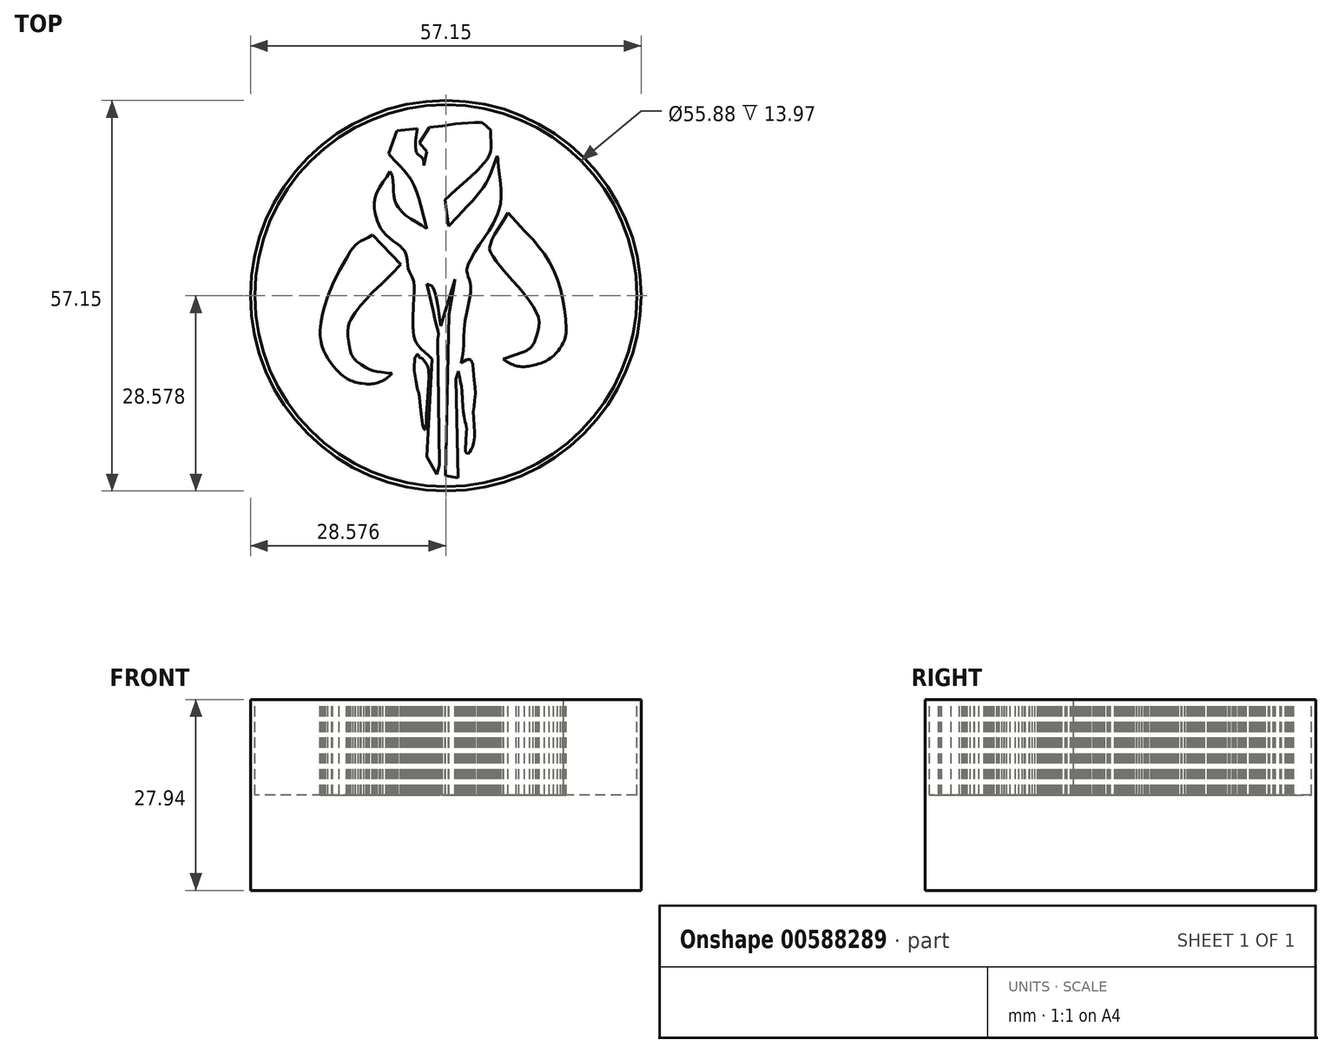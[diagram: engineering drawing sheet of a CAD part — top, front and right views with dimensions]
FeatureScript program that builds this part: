
annotation { "Feature Type Name" : "Feature", "Feature Type Description" : "" }
export const myFeature = defineFeature(function(context is Context, id is Id, definition is map)
    precondition{}
    {
        {
            var Q0;
            Q0=qCreatedBy(makeId("Top.planeOp"),FACE);
            var sketch = newSketch(context, id + "F0", { "sketchPlane" : qUnion([Q0])});
            skLineSegment(sketch, "E0", {"start": v(-3.17, -5.44) * mm, "end": v(-3.05, -5.48) * mm});
            skLineSegment(sketch, "E1", {"start": v(-3.05, -5.48) * mm, "end": v(-3, -5.51) * mm});
            skLineSegment(sketch, "E2", {"start": v(-3, -5.51) * mm, "end": v(-2.97, -5.54) * mm});
            skLineSegment(sketch, "E3", {"start": v(-2.97, -5.54) * mm, "end": v(-2.94, -5.6) * mm});
            skLineSegment(sketch, "E4", {"start": v(-2.94, -5.6) * mm, "end": v(-2.93, -5.66) * mm});
            skLineSegment(sketch, "E5", {"start": v(-2.93, -5.66) * mm, "end": v(-2.91, -5.76) * mm});
            skLineSegment(sketch, "E6", {"start": v(-2.91, -5.76) * mm, "end": v(-2.89, -5.81) * mm});
            skLineSegment(sketch, "E7", {"start": v(-2.89, -5.81) * mm, "end": v(-2.85, -5.86) * mm});
            skLineSegment(sketch, "E8", {"start": v(-2.85, -5.86) * mm, "end": v(-2.75, -5.91) * mm});
            skLineSegment(sketch, "E9", {"start": v(-2.75, -5.91) * mm, "end": v(-2.55, -5.98) * mm});
            skLineSegment(sketch, "E10", {"start": v(-2.55, -5.98) * mm, "end": v(-2.5, -6.01) * mm});
            skLineSegment(sketch, "E11", {"start": v(-2.5, -6.01) * mm, "end": v(-2.48, -6.03) * mm});
            skLineSegment(sketch, "E12", {"start": v(-2.48, -6.03) * mm, "end": v(-2.48, -6.03) * mm});
            skLineSegment(sketch, "E13", {"start": v(-2.48, -6.03) * mm, "end": v(-2.47, -6.04) * mm});
            skLineSegment(sketch, "E14", {"start": v(-2.47, -6.04) * mm, "end": v(-2.46, -6.05) * mm});
            skLineSegment(sketch, "E15", {"start": v(-2.46, -6.05) * mm, "end": v(-2.42, -6.08) * mm});
            skLineSegment(sketch, "E16", {"start": v(-2.42, -6.08) * mm, "end": v(-2.27, -6.23) * mm});
            skLineSegment(sketch, "E17", {"start": v(-2.27, -6.23) * mm, "end": v(-2, -6.56) * mm});
            skLineSegment(sketch, "E18", {"start": v(-2, -6.56) * mm, "end": v(-1.76, -6.92) * mm});
            skLineSegment(sketch, "E19", {"start": v(-1.76, -6.92) * mm, "end": v(-1.59, -7.32) * mm});
            skLineSegment(sketch, "E20", {"start": v(-1.59, -7.32) * mm, "end": v(-1.5, -7.74) * mm});
            skLineSegment(sketch, "E21", {"start": v(-1.5, -7.74) * mm, "end": v(-1.46, -8.75) * mm});
            skLineSegment(sketch, "E22", {"start": v(-1.46, -8.75) * mm, "end": v(-1.5, -9.75) * mm});
            skLineSegment(sketch, "E23", {"start": v(-1.5, -9.75) * mm, "end": v(-1.58, -10.76) * mm});
            skLineSegment(sketch, "E24", {"start": v(-1.58, -10.76) * mm, "end": v(-1.78, -13.47) * mm});
            skLineSegment(sketch, "E25", {"start": v(-1.78, -13.47) * mm, "end": v(-1.82, -14.2) * mm});
            skLineSegment(sketch, "E26", {"start": v(-1.82, -14.2) * mm, "end": v(-1.82, -14.94) * mm});
            skLineSegment(sketch, "E27", {"start": v(-1.82, -14.94) * mm, "end": v(-1.85, -15.67) * mm});
            skLineSegment(sketch, "E28", {"start": v(-1.85, -15.67) * mm, "end": v(-1.94, -16.21) * mm});
            skLineSegment(sketch, "E29", {"start": v(-1.94, -16.21) * mm, "end": v(-1.97, -16.33) * mm});
            skLineSegment(sketch, "E30", {"start": v(-1.97, -16.33) * mm, "end": v(-2.02, -16.45) * mm});
            skLineSegment(sketch, "E31", {"start": v(-2.02, -16.45) * mm, "end": v(-2.04, -16.47) * mm});
            skLineSegment(sketch, "E32", {"start": v(-2.04, -16.47) * mm, "end": v(-2.05, -16.47) * mm});
            skLineSegment(sketch, "E33", {"start": v(-2.05, -16.47) * mm, "end": v(-2.06, -16.47) * mm});
            skLineSegment(sketch, "E34", {"start": v(-2.06, -16.47) * mm, "end": v(-2.08, -16.47) * mm});
            skLineSegment(sketch, "E35", {"start": v(-2.08, -16.47) * mm, "end": v(-2.1, -16.46) * mm});
            skLineSegment(sketch, "E36", {"start": v(-2.1, -16.46) * mm, "end": v(-2.12, -16.43) * mm});
            skLineSegment(sketch, "E37", {"start": v(-2.12, -16.43) * mm, "end": v(-2.2, -16.26) * mm});
            skLineSegment(sketch, "E38", {"start": v(-2.2, -16.26) * mm, "end": v(-2.3, -15.9) * mm});
            skLineSegment(sketch, "E39", {"start": v(-2.3, -15.9) * mm, "end": v(-2.38, -15.55) * mm});
            skLineSegment(sketch, "E40", {"start": v(-2.38, -15.55) * mm, "end": v(-2.52, -14.6) * mm});
            skLineSegment(sketch, "E41", {"start": v(-2.52, -14.6) * mm, "end": v(-2.63, -13.64) * mm});
            skLineSegment(sketch, "E42", {"start": v(-2.63, -13.64) * mm, "end": v(-2.86, -11.73) * mm});
            skLineSegment(sketch, "E43", {"start": v(-2.86, -11.73) * mm, "end": v(-2.92, -11.25) * mm});
            skLineSegment(sketch, "E44", {"start": v(-2.92, -11.25) * mm, "end": v(-2.95, -11.02) * mm});
            skLineSegment(sketch, "E45", {"start": v(-2.95, -11.02) * mm, "end": v(-2.97, -10.9) * mm});
            skLineSegment(sketch, "E46", {"start": v(-2.97, -10.9) * mm, "end": v(-2.98, -10.88) * mm});
            skLineSegment(sketch, "E47", {"start": v(-2.98, -10.88) * mm, "end": v(-2.98, -10.87) * mm});
            skLineSegment(sketch, "E48", {"start": v(-2.98, -10.87) * mm, "end": v(-3.03, -10.84) * mm});
            skLineSegment(sketch, "E49", {"start": v(-3.03, -10.84) * mm, "end": v(-3.05, -10.82) * mm});
            skLineSegment(sketch, "E50", {"start": v(-3.05, -10.82) * mm, "end": v(-3.07, -10.8) * mm});
            skLineSegment(sketch, "E51", {"start": v(-3.07, -10.8) * mm, "end": v(-3.07, -10.8) * mm});
            skLineSegment(sketch, "E52", {"start": v(-3.07, -10.8) * mm, "end": v(-3.07, -10.77) * mm});
            skLineSegment(sketch, "E53", {"start": v(-3.07, -10.77) * mm, "end": v(-3.09, -10.7) * mm});
            skLineSegment(sketch, "E54", {"start": v(-3.09, -10.7) * mm, "end": v(-3.15, -10.43) * mm});
            skLineSegment(sketch, "E55", {"start": v(-3.15, -10.43) * mm, "end": v(-3.37, -9.34) * mm});
            skLineSegment(sketch, "E56", {"start": v(-3.37, -9.34) * mm, "end": v(-3.5, -8.6) * mm});
            skLineSegment(sketch, "E57", {"start": v(-3.5, -8.6) * mm, "end": v(-3.59, -7.84) * mm});
            skLineSegment(sketch, "E58", {"start": v(-3.59, -7.84) * mm, "end": v(-3.63, -7.09) * mm});
            skLineSegment(sketch, "E59", {"start": v(-3.63, -7.09) * mm, "end": v(-3.57, -6.34) * mm});
            skLineSegment(sketch, "E60", {"start": v(-3.57, -6.34) * mm, "end": v(-3.5, -6.07) * mm});
            skLineSegment(sketch, "E61", {"start": v(-3.5, -6.07) * mm, "end": v(-3.42, -5.81) * mm});
            skLineSegment(sketch, "E62", {"start": v(-3.42, -5.81) * mm, "end": v(-3.3, -5.61) * mm});
            skLineSegment(sketch, "E63", {"start": v(-3.3, -5.61) * mm, "end": v(-3.17, -5.44) * mm});
            skLineSegment(sketch, "E64", {"start": v(8.53, 23.62) * mm, "end": v(8.6, 23.33) * mm});
            skLineSegment(sketch, "E65", {"start": v(8.6, 23.33) * mm, "end": v(8.62, 23.18) * mm});
            skLineSegment(sketch, "E66", {"start": v(8.62, 23.18) * mm, "end": v(8.63, 23.03) * mm});
            skLineSegment(sketch, "E67", {"start": v(8.63, 23.03) * mm, "end": v(8.63, 23.03) * mm});
            skLineSegment(sketch, "E68", {"start": v(8.63, 23.03) * mm, "end": v(8.63, 23) * mm});
            skLineSegment(sketch, "E69", {"start": v(8.63, 23) * mm, "end": v(8.64, 22.93) * mm});
            skLineSegment(sketch, "E70", {"start": v(8.64, 22.93) * mm, "end": v(8.65, 22.63) * mm});
            skLineSegment(sketch, "E71", {"start": v(8.65, 22.63) * mm, "end": v(8.77, 21.44) * mm});
            skLineSegment(sketch, "E72", {"start": v(8.77, 21.44) * mm, "end": v(8.89, 20.48) * mm});
            skLineSegment(sketch, "E73", {"start": v(8.89, 20.48) * mm, "end": v(9, 19.52) * mm});
            skLineSegment(sketch, "E74", {"start": v(9, 19.52) * mm, "end": v(9.08, 18.56) * mm});
            skLineSegment(sketch, "E75", {"start": v(9.08, 18.56) * mm, "end": v(9.1, 17.6) * mm});
            skLineSegment(sketch, "E76", {"start": v(9.1, 17.6) * mm, "end": v(9.01, 16.64) * mm});
            skLineSegment(sketch, "E77", {"start": v(9.01, 16.64) * mm, "end": v(8.85, 15.87) * mm});
            skLineSegment(sketch, "E78", {"start": v(8.85, 15.87) * mm, "end": v(8.6, 15.12) * mm});
            skLineSegment(sketch, "E79", {"start": v(8.6, 15.12) * mm, "end": v(8.3, 14.38) * mm});
            skLineSegment(sketch, "E80", {"start": v(8.3, 14.38) * mm, "end": v(7.94, 13.68) * mm});
            skLineSegment(sketch, "E81", {"start": v(7.94, 13.68) * mm, "end": v(7.3, 12.62) * mm});
            skLineSegment(sketch, "E82", {"start": v(7.3, 12.62) * mm, "end": v(6.62, 11.6) * mm});
            skLineSegment(sketch, "E83", {"start": v(6.62, 11.6) * mm, "end": v(5.92, 10.57) * mm});
            skLineSegment(sketch, "E84", {"start": v(5.92, 10.57) * mm, "end": v(5.25, 9.53) * mm});
            skLineSegment(sketch, "E85", {"start": v(5.25, 9.53) * mm, "end": v(4.65, 8.45) * mm});
            skLineSegment(sketch, "E86", {"start": v(4.65, 8.45) * mm, "end": v(4.36, 7.86) * mm});
            skLineSegment(sketch, "E87", {"start": v(4.36, 7.86) * mm, "end": v(4.14, 7.24) * mm});
            skLineSegment(sketch, "E88", {"start": v(4.14, 7.24) * mm, "end": v(4.1, 6.96) * mm});
            skLineSegment(sketch, "E89", {"start": v(4.1, 6.96) * mm, "end": v(4.1, 6.68) * mm});
            skLineSegment(sketch, "E90", {"start": v(4.1, 6.68) * mm, "end": v(4.17, 6.31) * mm});
            skLineSegment(sketch, "E91", {"start": v(4.17, 6.31) * mm, "end": v(4.28, 5.96) * mm});
            skLineSegment(sketch, "E92", {"start": v(4.28, 5.96) * mm, "end": v(4.45, 5.49) * mm});
            skLineSegment(sketch, "E93", {"start": v(4.45, 5.49) * mm, "end": v(4.6, 5.02) * mm});
            skLineSegment(sketch, "E94", {"start": v(4.6, 5.02) * mm, "end": v(4.67, 4.53) * mm});
            skLineSegment(sketch, "E95", {"start": v(4.67, 4.53) * mm, "end": v(4.63, 3.56) * mm});
            skLineSegment(sketch, "E96", {"start": v(4.63, 3.56) * mm, "end": v(4.48, 2.6) * mm});
            skLineSegment(sketch, "E97", {"start": v(4.48, 2.6) * mm, "end": v(4.26, 1.63) * mm});
            skLineSegment(sketch, "E98", {"start": v(4.26, 1.63) * mm, "end": v(4.05, 0.68) * mm});
            skLineSegment(sketch, "E99", {"start": v(4.05, 0.68) * mm, "end": v(3.85, -0.55) * mm});
            skLineSegment(sketch, "E100", {"start": v(3.85, -0.55) * mm, "end": v(3.72, -1.78) * mm});
            skLineSegment(sketch, "E101", {"start": v(3.72, -1.78) * mm, "end": v(3.66, -3.03) * mm});
            skLineSegment(sketch, "E102", {"start": v(3.66, -3.03) * mm, "end": v(3.64, -3.96) * mm});
            skLineSegment(sketch, "E103", {"start": v(3.64, -3.96) * mm, "end": v(3.58, -4.9) * mm});
            skLineSegment(sketch, "E104", {"start": v(3.58, -4.9) * mm, "end": v(3.47, -5.82) * mm});
            skLineSegment(sketch, "E105", {"start": v(3.47, -5.82) * mm, "end": v(3.27, -6.73) * mm});
            skLineSegment(sketch, "E106", {"start": v(1.4, 13.3) * mm, "end": v(2.74, 14.74) * mm});
            skLineSegment(sketch, "E107", {"start": v(2.74, 14.74) * mm, "end": v(4.1, 16.14) * mm});
            skLineSegment(sketch, "E108", {"start": v(4.1, 16.14) * mm, "end": v(4.94, 17.05) * mm});
            skLineSegment(sketch, "E109", {"start": v(4.94, 17.05) * mm, "end": v(5.75, 18) * mm});
            skLineSegment(sketch, "E110", {"start": v(5.75, 18) * mm, "end": v(6.5, 18.98) * mm});
            skLineSegment(sketch, "E111", {"start": v(6.5, 18.98) * mm, "end": v(6.93, 19.69) * mm});
            skLineSegment(sketch, "E112", {"start": v(6.93, 19.69) * mm, "end": v(7.3, 20.44) * mm});
            skLineSegment(sketch, "E113", {"start": v(7.3, 20.44) * mm, "end": v(7.63, 21.22) * mm});
            skLineSegment(sketch, "E114", {"start": v(7.63, 21.22) * mm, "end": v(8.07, 22.43) * mm});
            skLineSegment(sketch, "E115", {"start": v(8.07, 22.43) * mm, "end": v(8.53, 23.62) * mm});
            skLineSegment(sketch, "E116", {"start": v(0.9, 17.17) * mm, "end": v(1.4, 13.3) * mm});
            skLineSegment(sketch, "E117", {"start": v(7.54, 27.39) * mm, "end": v(7.55, 26.52) * mm});
            skLineSegment(sketch, "E118", {"start": v(7.55, 26.52) * mm, "end": v(7.6, 25.64) * mm});
            skLineSegment(sketch, "E119", {"start": v(7.6, 25.64) * mm, "end": v(7.61, 24.77) * mm});
            skLineSegment(sketch, "E120", {"start": v(7.61, 24.77) * mm, "end": v(7.54, 24.23) * mm});
            skLineSegment(sketch, "E121", {"start": v(7.54, 24.23) * mm, "end": v(7.39, 23.72) * mm});
            skLineSegment(sketch, "E122", {"start": v(7.39, 23.72) * mm, "end": v(7.06, 23.12) * mm});
            skLineSegment(sketch, "E123", {"start": v(7.06, 23.12) * mm, "end": v(6.65, 22.57) * mm});
            skLineSegment(sketch, "E124", {"start": v(6.65, 22.57) * mm, "end": v(5.67, 21.53) * mm});
            skLineSegment(sketch, "E125", {"start": v(5.67, 21.53) * mm, "end": v(4.63, 20.55) * mm});
            skLineSegment(sketch, "E126", {"start": v(4.63, 20.55) * mm, "end": v(3.55, 19.6) * mm});
            skLineSegment(sketch, "E127", {"start": v(3.55, 19.6) * mm, "end": v(2.48, 18.64) * mm});
            skLineSegment(sketch, "E128", {"start": v(2.48, 18.64) * mm, "end": v(0.9, 17.17) * mm});
            skLineSegment(sketch, "E129", {"start": v(-1.38, 27.79) * mm, "end": v(0.5, 28.01) * mm});
            skLineSegment(sketch, "E130", {"start": v(0.5, 28.01) * mm, "end": v(2.4, 28.27) * mm});
            skLineSegment(sketch, "E131", {"start": v(2.4, 28.27) * mm, "end": v(3.34, 28.38) * mm});
            skLineSegment(sketch, "E132", {"start": v(3.34, 28.38) * mm, "end": v(4.29, 28.46) * mm});
            skLineSegment(sketch, "E133", {"start": v(4.29, 28.46) * mm, "end": v(5.23, 28.5) * mm});
            skLineSegment(sketch, "E134", {"start": v(5.23, 28.5) * mm, "end": v(5.99, 28.48) * mm});
            skLineSegment(sketch, "E135", {"start": v(5.99, 28.48) * mm, "end": v(6.2, 28.46) * mm});
            skLineSegment(sketch, "E136", {"start": v(6.2, 28.46) * mm, "end": v(6.39, 28.4) * mm});
            skLineSegment(sketch, "E137", {"start": v(6.39, 28.4) * mm, "end": v(6.6, 28.26) * mm});
            skLineSegment(sketch, "E138", {"start": v(6.6, 28.26) * mm, "end": v(6.8, 28.1) * mm});
            skLineSegment(sketch, "E139", {"start": v(6.8, 28.1) * mm, "end": v(7.16, 27.73) * mm});
            skLineSegment(sketch, "E140", {"start": v(7.16, 27.73) * mm, "end": v(7.54, 27.39) * mm});
            skLineSegment(sketch, "E141", {"start": v(-2.87, 25.5) * mm, "end": v(-1.38, 27.79) * mm});
            skLineSegment(sketch, "E142", {"start": v(-1.78, 24.22) * mm, "end": v(-2.87, 25.5) * mm});
            skLineSegment(sketch, "E143", {"start": v(-2.18, 22.23) * mm, "end": v(-1.78, 24.22) * mm});
            skLineSegment(sketch, "E144", {"start": v(-3.17, 27.59) * mm, "end": v(-3.27, 26.71) * mm});
            skLineSegment(sketch, "E145", {"start": v(-3.27, 26.71) * mm, "end": v(-3.39, 25.83) * mm});
            skLineSegment(sketch, "E146", {"start": v(-3.39, 25.83) * mm, "end": v(-3.44, 24.96) * mm});
            skLineSegment(sketch, "E147", {"start": v(-3.44, 24.96) * mm, "end": v(-3.38, 24.38) * mm});
            skLineSegment(sketch, "E148", {"start": v(-3.38, 24.38) * mm, "end": v(-3.27, 24.08) * mm});
            skLineSegment(sketch, "E149", {"start": v(-3.27, 24.08) * mm, "end": v(-3.15, 23.93) * mm});
            skLineSegment(sketch, "E150", {"start": v(-3.15, 23.93) * mm, "end": v(-3, 23.8) * mm});
            skLineSegment(sketch, "E151", {"start": v(-3, 23.8) * mm, "end": v(-2.68, 23.55) * mm});
            skLineSegment(sketch, "E152", {"start": v(-2.68, 23.55) * mm, "end": v(-2.38, 23.27) * mm});
            skLineSegment(sketch, "E153", {"start": v(-2.38, 23.27) * mm, "end": v(-2.24, 23.05) * mm});
            skLineSegment(sketch, "E154", {"start": v(-2.24, 23.05) * mm, "end": v(-2.19, 22.8) * mm});
            skLineSegment(sketch, "E155", {"start": v(-2.19, 22.8) * mm, "end": v(-2.19, 22.51) * mm});
            skLineSegment(sketch, "E156", {"start": v(-2.19, 22.51) * mm, "end": v(-2.18, 22.23) * mm});
            skLineSegment(sketch, "E157", {"start": v(-6.14, 27.3) * mm, "end": v(-3.17, 27.59) * mm});
            skLineSegment(sketch, "E158", {"start": v(-7.34, 23.92) * mm, "end": v(-6.14, 27.3) * mm});
            skLineSegment(sketch, "E159", {"start": v(-1.78, 12.9) * mm, "end": v(-2.23, 14.64) * mm});
            skLineSegment(sketch, "E160", {"start": v(-2.23, 14.64) * mm, "end": v(-2.65, 16.38) * mm});
            skLineSegment(sketch, "E161", {"start": v(-2.65, 16.38) * mm, "end": v(-2.91, 17.34) * mm});
            skLineSegment(sketch, "E162", {"start": v(-2.91, 17.34) * mm, "end": v(-3.22, 18.28) * mm});
            skLineSegment(sketch, "E163", {"start": v(-3.22, 18.28) * mm, "end": v(-3.6, 19.22) * mm});
            skLineSegment(sketch, "E164", {"start": v(-3.6, 19.22) * mm, "end": v(-4.08, 20.1) * mm});
            skLineSegment(sketch, "E165", {"start": v(-4.08, 20.1) * mm, "end": v(-4.55, 20.8) * mm});
            skLineSegment(sketch, "E166", {"start": v(-4.55, 20.8) * mm, "end": v(-5.08, 21.44) * mm});
            skLineSegment(sketch, "E167", {"start": v(-5.08, 21.44) * mm, "end": v(-5.64, 22.06) * mm});
            skLineSegment(sketch, "E168", {"start": v(-5.64, 22.06) * mm, "end": v(-6.5, 22.98) * mm});
            skLineSegment(sketch, "E169", {"start": v(-6.5, 22.98) * mm, "end": v(-7.34, 23.92) * mm});
            skLineSegment(sketch, "E170", {"start": v(-7.14, 21.34) * mm, "end": v(-6.97, 21.05) * mm});
            skLineSegment(sketch, "E171", {"start": v(-6.97, 21.05) * mm, "end": v(-6.89, 20.9) * mm});
            skLineSegment(sketch, "E172", {"start": v(-6.89, 20.9) * mm, "end": v(-6.86, 20.82) * mm});
            skLineSegment(sketch, "E173", {"start": v(-6.86, 20.82) * mm, "end": v(-6.85, 20.78) * mm});
            skLineSegment(sketch, "E174", {"start": v(-6.85, 20.78) * mm, "end": v(-6.84, 20.76) * mm});
            skLineSegment(sketch, "E175", {"start": v(-6.84, 20.76) * mm, "end": v(-6.84, 20.75) * mm});
            skLineSegment(sketch, "E176", {"start": v(-6.84, 20.75) * mm, "end": v(-6.84, 20.74) * mm});
            skLineSegment(sketch, "E177", {"start": v(-6.84, 20.74) * mm, "end": v(-6.84, 20.73) * mm});
            skLineSegment(sketch, "E178", {"start": v(-6.84, 20.73) * mm, "end": v(-6.83, 20.7) * mm});
            skLineSegment(sketch, "E179", {"start": v(-6.83, 20.7) * mm, "end": v(-6.8, 20.53) * mm});
            skLineSegment(sketch, "E180", {"start": v(-6.8, 20.53) * mm, "end": v(-6.72, 19.85) * mm});
            skLineSegment(sketch, "E181", {"start": v(-6.72, 19.85) * mm, "end": v(-6.68, 19.17) * mm});
            skLineSegment(sketch, "E182", {"start": v(-6.68, 19.17) * mm, "end": v(-6.65, 18.49) * mm});
            skLineSegment(sketch, "E183", {"start": v(-6.65, 18.49) * mm, "end": v(-6.58, 17.81) * mm});
            skLineSegment(sketch, "E184", {"start": v(-6.58, 17.81) * mm, "end": v(-6.46, 17.15) * mm});
            skLineSegment(sketch, "E185", {"start": v(-6.46, 17.15) * mm, "end": v(-6.26, 16.6) * mm});
            skLineSegment(sketch, "E186", {"start": v(-6.26, 16.6) * mm, "end": v(-5.98, 16.08) * mm});
            skLineSegment(sketch, "E187", {"start": v(-5.98, 16.08) * mm, "end": v(-5.46, 15.46) * mm});
            skLineSegment(sketch, "E188", {"start": v(-5.46, 15.46) * mm, "end": v(-4.85, 14.93) * mm});
            skLineSegment(sketch, "E189", {"start": v(-4.85, 14.93) * mm, "end": v(-4.1, 14.4) * mm});
            skLineSegment(sketch, "E190", {"start": v(-4.1, 14.4) * mm, "end": v(-3.32, 13.92) * mm});
            skLineSegment(sketch, "E191", {"start": v(-3.32, 13.92) * mm, "end": v(-2.54, 13.44) * mm});
            skLineSegment(sketch, "E192", {"start": v(-2.54, 13.44) * mm, "end": v(-1.78, 12.9) * mm});
            skLineSegment(sketch, "E193", {"start": v(-0.99, -6.13) * mm, "end": v(-1.48, -5.63) * mm});
            skLineSegment(sketch, "E194", {"start": v(-1.48, -5.63) * mm, "end": v(-2.01, -5.17) * mm});
            skLineSegment(sketch, "E195", {"start": v(-2.01, -5.17) * mm, "end": v(-2.56, -4.68) * mm});
            skLineSegment(sketch, "E196", {"start": v(-2.56, -4.68) * mm, "end": v(-3.06, -4.15) * mm});
            skLineSegment(sketch, "E197", {"start": v(-3.06, -4.15) * mm, "end": v(-3.3, -3.79) * mm});
            skLineSegment(sketch, "E198", {"start": v(-3.3, -3.79) * mm, "end": v(-3.5, -3.4) * mm});
            skLineSegment(sketch, "E199", {"start": v(-3.5, -3.4) * mm, "end": v(-3.67, -2.76) * mm});
            skLineSegment(sketch, "E200", {"start": v(-3.67, -2.76) * mm, "end": v(-3.76, -2.1) * mm});
            skLineSegment(sketch, "E201", {"start": v(-3.76, -2.1) * mm, "end": v(-3.8, -1.43) * mm});
            skLineSegment(sketch, "E202", {"start": v(-3.8, -1.43) * mm, "end": v(-3.81, 0.04) * mm});
            skLineSegment(sketch, "E203", {"start": v(-3.81, 0.04) * mm, "end": v(-3.73, 1.52) * mm});
            skLineSegment(sketch, "E204", {"start": v(-3.73, 1.52) * mm, "end": v(-3.64, 2.99) * mm});
            skLineSegment(sketch, "E205", {"start": v(-3.64, 2.99) * mm, "end": v(-3.61, 3.72) * mm});
            skLineSegment(sketch, "E206", {"start": v(-3.61, 3.72) * mm, "end": v(-3.61, 4.46) * mm});
            skLineSegment(sketch, "E207", {"start": v(-3.61, 4.46) * mm, "end": v(-3.68, 5.19) * mm});
            skLineSegment(sketch, "E208", {"start": v(-3.68, 5.19) * mm, "end": v(-3.77, 5.55) * mm});
            skLineSegment(sketch, "E209", {"start": v(-3.77, 5.55) * mm, "end": v(-3.92, 5.9) * mm});
            skLineSegment(sketch, "E210", {"start": v(-3.92, 5.9) * mm, "end": v(-4.1, 6.23) * mm});
            skLineSegment(sketch, "E211", {"start": v(-4.1, 6.23) * mm, "end": v(-4.3, 6.66) * mm});
            skLineSegment(sketch, "E212", {"start": v(-4.3, 6.66) * mm, "end": v(-4.46, 7.1) * mm});
            skLineSegment(sketch, "E213", {"start": v(-4.46, 7.1) * mm, "end": v(-4.57, 7.56) * mm});
            skLineSegment(sketch, "E214", {"start": v(-4.57, 7.56) * mm, "end": v(-4.64, 8.29) * mm});
            skLineSegment(sketch, "E215", {"start": v(-4.64, 8.29) * mm, "end": v(-4.75, 9.01) * mm});
            skLineSegment(sketch, "E216", {"start": v(-4.75, 9.01) * mm, "end": v(-4.85, 9.35) * mm});
            skLineSegment(sketch, "E217", {"start": v(-4.85, 9.35) * mm, "end": v(-5.01, 9.67) * mm});
            skLineSegment(sketch, "E218", {"start": v(-5.01, 9.67) * mm, "end": v(-5.3, 10.04) * mm});
            skLineSegment(sketch, "E219", {"start": v(-5.3, 10.04) * mm, "end": v(-5.63, 10.36) * mm});
            skLineSegment(sketch, "E220", {"start": v(-5.63, 10.36) * mm, "end": v(-6.16, 10.78) * mm});
            skLineSegment(sketch, "E221", {"start": v(-6.16, 10.78) * mm, "end": v(-6.7, 11.19) * mm});
            skLineSegment(sketch, "E222", {"start": v(-6.7, 11.19) * mm, "end": v(-7.24, 11.6) * mm});
            skLineSegment(sketch, "E223", {"start": v(-7.24, 11.6) * mm, "end": v(-7.74, 12.04) * mm});
            skLineSegment(sketch, "E224", {"start": v(-7.74, 12.04) * mm, "end": v(-8.18, 12.52) * mm});
            skLineSegment(sketch, "E225", {"start": v(-8.18, 12.52) * mm, "end": v(-8.54, 13.07) * mm});
            skLineSegment(sketch, "E226", {"start": v(-8.54, 13.07) * mm, "end": v(-8.99, 14.08) * mm});
            skLineSegment(sketch, "E227", {"start": v(-8.99, 14.08) * mm, "end": v(-9.3, 15.15) * mm});
            skLineSegment(sketch, "E228", {"start": v(-9.3, 15.15) * mm, "end": v(-9.43, 15.98) * mm});
            skLineSegment(sketch, "E229", {"start": v(-9.43, 15.98) * mm, "end": v(-9.44, 16.81) * mm});
            skLineSegment(sketch, "E230", {"start": v(-9.44, 16.81) * mm, "end": v(-9.33, 17.5) * mm});
            skLineSegment(sketch, "E231", {"start": v(-9.33, 17.5) * mm, "end": v(-9.11, 18.16) * mm});
            skLineSegment(sketch, "E232", {"start": v(-9.11, 18.16) * mm, "end": v(-8.68, 18.98) * mm});
            skLineSegment(sketch, "E233", {"start": v(-8.68, 18.98) * mm, "end": v(-8.16, 19.76) * mm});
            skLineSegment(sketch, "E234", {"start": v(-8.16, 19.76) * mm, "end": v(-7.62, 20.54) * mm});
            skLineSegment(sketch, "E235", {"start": v(-7.62, 20.54) * mm, "end": v(-7.14, 21.34) * mm});
            skLineSegment(sketch, "E236", {"start": v(-1.78, -20.42) * mm, "end": v(-0.99, -6.13) * mm});
            skLineSegment(sketch, "E237", {"start": v(-0.3, -23) * mm, "end": v(-1.78, -20.42) * mm});
            skLineSegment(sketch, "E238", {"start": v(0.1, -21.6) * mm, "end": v(-0.3, -23) * mm});
            skLineSegment(sketch, "E239", {"start": v(-0.2, -3.26) * mm, "end": v(0.1, -21.6) * mm});
            skLineSegment(sketch, "E240", {"start": v(-1.78, 4.88) * mm, "end": v(-0.83, 0.85) * mm});
            skLineSegment(sketch, "E241", {"start": v(-0.83, 0.85) * mm, "end": v(-0.6, -0.16) * mm});
            skLineSegment(sketch, "E242", {"start": v(-0.6, -0.16) * mm, "end": v(-0.35, -1.17) * mm});
            skLineSegment(sketch, "E243", {"start": v(-0.35, -1.17) * mm, "end": v(-0.22, -1.61) * mm});
            skLineSegment(sketch, "E244", {"start": v(-0.22, -1.61) * mm, "end": v(-0.1, -2.06) * mm});
            skLineSegment(sketch, "E245", {"start": v(-0.1, -2.06) * mm, "end": v(-0.08, -2.5) * mm});
            skLineSegment(sketch, "E246", {"start": v(-0.08, -2.5) * mm, "end": v(-0.2, -3.26) * mm});
            skLineSegment(sketch, "E247", {"start": v(0.3, -1.27) * mm, "end": v(0.1, 0.07) * mm});
            skLineSegment(sketch, "E248", {"start": v(0.1, 0.07) * mm, "end": v(-0.12, 1.41) * mm});
            skLineSegment(sketch, "E249", {"start": v(-0.12, 1.41) * mm, "end": v(-0.38, 2.75) * mm});
            skLineSegment(sketch, "E250", {"start": v(-0.38, 2.75) * mm, "end": v(-0.5, 3.33) * mm});
            skLineSegment(sketch, "E251", {"start": v(-0.5, 3.33) * mm, "end": v(-0.66, 3.9) * mm});
            skLineSegment(sketch, "E252", {"start": v(-0.66, 3.9) * mm, "end": v(-0.88, 4.37) * mm});
            skLineSegment(sketch, "E253", {"start": v(-0.88, 4.37) * mm, "end": v(-1.01, 4.52) * mm});
            skLineSegment(sketch, "E254", {"start": v(-1.01, 4.52) * mm, "end": v(-1.26, 4.66) * mm});
            skLineSegment(sketch, "E255", {"start": v(-1.26, 4.66) * mm, "end": v(-1.52, 4.76) * mm});
            skLineSegment(sketch, "E256", {"start": v(-1.52, 4.76) * mm, "end": v(-1.78, 4.88) * mm});
            skLineSegment(sketch, "E257", {"start": v(2.38, 5.57) * mm, "end": v(0.3, -1.27) * mm});
            skLineSegment(sketch, "E258", {"start": v(1.5, 0.41) * mm, "end": v(2.38, 5.57) * mm});
            skLineSegment(sketch, "E259", {"start": v(1, -23.2) * mm, "end": v(1.5, 0.41) * mm});
            skLineSegment(sketch, "E260", {"start": v(2.78, -23.5) * mm, "end": v(1, -23.2) * mm});
            skLineSegment(sketch, "E261", {"start": v(2.48, -9.01) * mm, "end": v(2.78, -23.5) * mm});
            skLineSegment(sketch, "E262", {"start": v(2.88, -7.87) * mm, "end": v(2.48, -9.01) * mm});
            skLineSegment(sketch, "E263", {"start": v(4.27, -20.02) * mm, "end": v(4.06, -19.87) * mm});
            skLineSegment(sketch, "E264", {"start": v(4.06, -19.87) * mm, "end": v(3.95, -19.79) * mm});
            skLineSegment(sketch, "E265", {"start": v(3.95, -19.79) * mm, "end": v(3.9, -19.72) * mm});
            skLineSegment(sketch, "E266", {"start": v(3.9, -19.72) * mm, "end": v(3.88, -19.65) * mm});
            skLineSegment(sketch, "E267", {"start": v(3.88, -19.65) * mm, "end": v(3.87, -19.64) * mm});
            skLineSegment(sketch, "E268", {"start": v(3.87, -19.64) * mm, "end": v(3.87, -19.63) * mm});
            skLineSegment(sketch, "E269", {"start": v(3.87, -19.63) * mm, "end": v(3.87, -19.62) * mm});
            skLineSegment(sketch, "E270", {"start": v(3.87, -19.62) * mm, "end": v(3.87, -19.62) * mm});
            skLineSegment(sketch, "E271", {"start": v(3.87, -19.62) * mm, "end": v(3.87, -19.6) * mm});
            skLineSegment(sketch, "E272", {"start": v(3.87, -19.6) * mm, "end": v(3.87, -19.54) * mm});
            skLineSegment(sketch, "E273", {"start": v(3.87, -19.54) * mm, "end": v(3.87, -19.27) * mm});
            skLineSegment(sketch, "E274", {"start": v(3.87, -19.27) * mm, "end": v(3.93, -18.2) * mm});
            skLineSegment(sketch, "E275", {"start": v(3.93, -18.2) * mm, "end": v(4.05, -16.76) * mm});
            skLineSegment(sketch, "E276", {"start": v(4.05, -16.76) * mm, "end": v(4.07, -16.39) * mm});
            skLineSegment(sketch, "E277", {"start": v(4.07, -16.39) * mm, "end": v(4.05, -16.03) * mm});
            skLineSegment(sketch, "E278", {"start": v(4.05, -16.03) * mm, "end": v(3.96, -15.67) * mm});
            skLineSegment(sketch, "E279", {"start": v(3.96, -15.67) * mm, "end": v(3.85, -15.32) * mm});
            skLineSegment(sketch, "E280", {"start": v(3.85, -15.32) * mm, "end": v(3.68, -14.6) * mm});
            skLineSegment(sketch, "E281", {"start": v(3.68, -14.6) * mm, "end": v(3.58, -13.85) * mm});
            skLineSegment(sketch, "E282", {"start": v(3.58, -13.85) * mm, "end": v(3.53, -13.1) * mm});
            skLineSegment(sketch, "E283", {"start": v(3.53, -13.1) * mm, "end": v(3.37, -10.89) * mm});
            skLineSegment(sketch, "E284", {"start": v(3.37, -10.89) * mm, "end": v(3.28, -10.13) * mm});
            skLineSegment(sketch, "E285", {"start": v(3.28, -10.13) * mm, "end": v(3.15, -9.38) * mm});
            skLineSegment(sketch, "E286", {"start": v(3.15, -9.38) * mm, "end": v(3.03, -8.88) * mm});
            skLineSegment(sketch, "E287", {"start": v(3.03, -8.88) * mm, "end": v(2.93, -8.38) * mm});
            skLineSegment(sketch, "E288", {"start": v(2.93, -8.38) * mm, "end": v(2.88, -7.87) * mm});
            skLineSegment(sketch, "E289", {"start": v(3.27, -6.73) * mm, "end": v(3.44, -6.62) * mm});
            skLineSegment(sketch, "E290", {"start": v(3.44, -6.62) * mm, "end": v(3.53, -6.56) * mm});
            skLineSegment(sketch, "E291", {"start": v(3.53, -6.56) * mm, "end": v(3.57, -6.53) * mm});
            skLineSegment(sketch, "E292", {"start": v(3.57, -6.53) * mm, "end": v(3.57, -6.53) * mm});
            skLineSegment(sketch, "E293", {"start": v(3.57, -6.53) * mm, "end": v(3.58, -6.53) * mm});
            skLineSegment(sketch, "E294", {"start": v(3.58, -6.53) * mm, "end": v(3.6, -6.51) * mm});
            skLineSegment(sketch, "E295", {"start": v(3.6, -6.51) * mm, "end": v(3.69, -6.45) * mm});
            skLineSegment(sketch, "E296", {"start": v(3.69, -6.45) * mm, "end": v(4.05, -6.25) * mm});
            skLineSegment(sketch, "E297", {"start": v(4.05, -6.25) * mm, "end": v(4.29, -6.18) * mm});
            skLineSegment(sketch, "E298", {"start": v(4.29, -6.18) * mm, "end": v(4.45, -6.18) * mm});
            skLineSegment(sketch, "E299", {"start": v(4.45, -6.18) * mm, "end": v(4.59, -6.22) * mm});
            skLineSegment(sketch, "E300", {"start": v(4.59, -6.22) * mm, "end": v(4.7, -6.3) * mm});
            skLineSegment(sketch, "E301", {"start": v(4.7, -6.3) * mm, "end": v(4.8, -6.48) * mm});
            skLineSegment(sketch, "E302", {"start": v(4.8, -6.48) * mm, "end": v(4.9, -6.72) * mm});
            skLineSegment(sketch, "E303", {"start": v(4.9, -6.72) * mm, "end": v(4.94, -6.97) * mm});
            skLineSegment(sketch, "E304", {"start": v(4.94, -6.97) * mm, "end": v(5.02, -7.72) * mm});
            skLineSegment(sketch, "E305", {"start": v(5.02, -7.72) * mm, "end": v(5.07, -8.46) * mm});
            skLineSegment(sketch, "E306", {"start": v(5.07, -8.46) * mm, "end": v(5.16, -9.2) * mm});
            skLineSegment(sketch, "E307", {"start": v(5.16, -9.2) * mm, "end": v(5.3, -10.2) * mm});
            skLineSegment(sketch, "E308", {"start": v(5.3, -10.2) * mm, "end": v(5.33, -11.22) * mm});
            skLineSegment(sketch, "E309", {"start": v(5.33, -11.22) * mm, "end": v(5.25, -12.23) * mm});
            skLineSegment(sketch, "E310", {"start": v(5.25, -12.23) * mm, "end": v(5.13, -13.02) * mm});
            skLineSegment(sketch, "E311", {"start": v(5.13, -13.02) * mm, "end": v(5.06, -13.8) * mm});
            skLineSegment(sketch, "E312", {"start": v(5.06, -13.8) * mm, "end": v(5.09, -14.81) * mm});
            skLineSegment(sketch, "E313", {"start": v(5.09, -14.81) * mm, "end": v(5.17, -15.82) * mm});
            skLineSegment(sketch, "E314", {"start": v(5.17, -15.82) * mm, "end": v(5.22, -16.82) * mm});
            skLineSegment(sketch, "E315", {"start": v(5.22, -16.82) * mm, "end": v(5.2, -17.56) * mm});
            skLineSegment(sketch, "E316", {"start": v(5.2, -17.56) * mm, "end": v(5.12, -18.29) * mm});
            skLineSegment(sketch, "E317", {"start": v(5.12, -18.29) * mm, "end": v(4.97, -18.86) * mm});
            skLineSegment(sketch, "E318", {"start": v(4.97, -18.86) * mm, "end": v(4.74, -19.4) * mm});
            skLineSegment(sketch, "E319", {"start": v(4.74, -19.4) * mm, "end": v(4.52, -19.72) * mm});
            skLineSegment(sketch, "E320", {"start": v(4.52, -19.72) * mm, "end": v(4.27, -20.02) * mm});
            skLineSegment(sketch, "E321", {"start": v(-9.72, 12.02) * mm, "end": v(-5.55, 7.75) * mm});
            skLineSegment(sketch, "E322", {"start": v(-15.04, -7.61) * mm, "end": v(-15.65, -6.85) * mm});
            skLineSegment(sketch, "E323", {"start": v(-15.65, -6.85) * mm, "end": v(-16.22, -6.06) * mm});
            skLineSegment(sketch, "E324", {"start": v(-16.22, -6.06) * mm, "end": v(-16.58, -5.46) * mm});
            skLineSegment(sketch, "E325", {"start": v(-16.58, -5.46) * mm, "end": v(-16.9, -4.83) * mm});
            skLineSegment(sketch, "E326", {"start": v(-16.9, -4.83) * mm, "end": v(-17.13, -4.16) * mm});
            skLineSegment(sketch, "E327", {"start": v(-17.13, -4.16) * mm, "end": v(-17.28, -3.45) * mm});
            skLineSegment(sketch, "E328", {"start": v(-17.28, -3.45) * mm, "end": v(-17.35, -2.72) * mm});
            skLineSegment(sketch, "E329", {"start": v(-17.35, -2.72) * mm, "end": v(-17.37, -1.98) * mm});
            skLineSegment(sketch, "E330", {"start": v(-17.37, -1.98) * mm, "end": v(-17.28, -0.87) * mm});
            skLineSegment(sketch, "E331", {"start": v(-17.28, -0.87) * mm, "end": v(-17.1, 0.23) * mm});
            skLineSegment(sketch, "E332", {"start": v(-17.1, 0.23) * mm, "end": v(-16.83, 1.31) * mm});
            skLineSegment(sketch, "E333", {"start": v(-16.83, 1.31) * mm, "end": v(-16.26, 3.08) * mm});
            skLineSegment(sketch, "E334", {"start": v(-16.26, 3.08) * mm, "end": v(-15.57, 4.8) * mm});
            skLineSegment(sketch, "E335", {"start": v(-15.57, 4.8) * mm, "end": v(-14.61, 6.76) * mm});
            skLineSegment(sketch, "E336", {"start": v(-14.61, 6.76) * mm, "end": v(-13.53, 8.65) * mm});
            skLineSegment(sketch, "E337", {"start": v(-13.53, 8.65) * mm, "end": v(-13.22, 9.16) * mm});
            skLineSegment(sketch, "E338", {"start": v(-13.22, 9.16) * mm, "end": v(-12.9, 9.68) * mm});
            skLineSegment(sketch, "E339", {"start": v(-12.9, 9.68) * mm, "end": v(-12.57, 10.16) * mm});
            skLineSegment(sketch, "E340", {"start": v(-12.57, 10.16) * mm, "end": v(-12.17, 10.6) * mm});
            skLineSegment(sketch, "E341", {"start": v(-12.17, 10.6) * mm, "end": v(-11.8, 10.9) * mm});
            skLineSegment(sketch, "E342", {"start": v(-11.8, 10.9) * mm, "end": v(-11.4, 11.14) * mm});
            skLineSegment(sketch, "E343", {"start": v(-11.4, 11.14) * mm, "end": v(-11, 11.35) * mm});
            skLineSegment(sketch, "E344", {"start": v(-11, 11.35) * mm, "end": v(-10.35, 11.66) * mm});
            skLineSegment(sketch, "E345", {"start": v(-10.35, 11.66) * mm, "end": v(-9.72, 12.02) * mm});
            skArc(sketch, "E346", {"start": v(-11.27, -9.7) * mm, "mid": v(-13.36, -9.02) * mm, "end": v(-15.04, -7.61) * mm});
            skLineSegment(sketch, "E347", {"start": v(-10.76, -9.75) * mm, "end": v(-11.27, -9.7) * mm});
            skArc(sketch, "E348", {"start": v(-7.1, -8.48) * mm, "mid": v(-8.79, -9.53) * mm, "end": v(-10.76, -9.75) * mm});
            skLineSegment(sketch, "E349", {"start": v(-6.84, -8.22) * mm, "end": v(-7.1, -8.48) * mm});
            skLineSegment(sketch, "E350", {"start": v(-11.97, -6.48) * mm, "end": v(-11.33, -6.93) * mm});
            skLineSegment(sketch, "E351", {"start": v(-11.33, -6.93) * mm, "end": v(-10.66, -7.36) * mm});
            skLineSegment(sketch, "E352", {"start": v(-10.66, -7.36) * mm, "end": v(-10.17, -7.61) * mm});
            skLineSegment(sketch, "E353", {"start": v(-10.17, -7.61) * mm, "end": v(-9.65, -7.81) * mm});
            skLineSegment(sketch, "E354", {"start": v(-9.65, -7.81) * mm, "end": v(-9.08, -7.95) * mm});
            skLineSegment(sketch, "E355", {"start": v(-9.08, -7.95) * mm, "end": v(-8.5, -8.04) * mm});
            skLineSegment(sketch, "E356", {"start": v(-8.5, -8.04) * mm, "end": v(-7.67, -8.12) * mm});
            skLineSegment(sketch, "E357", {"start": v(-7.67, -8.12) * mm, "end": v(-6.84, -8.22) * mm});
            skArc(sketch, "E358", {"start": v(-12.99, -4.8) * mm, "mid": v(-12.65, -5.74) * mm, "end": v(-11.97, -6.48) * mm});
            skLineSegment(sketch, "E359", {"start": v(-5.55, 7.75) * mm, "end": v(-6.92, 6.32) * mm});
            skLineSegment(sketch, "E360", {"start": v(-6.92, 6.32) * mm, "end": v(-8.34, 4.94) * mm});
            skLineSegment(sketch, "E361", {"start": v(-8.34, 4.94) * mm, "end": v(-9.74, 3.57) * mm});
            skLineSegment(sketch, "E362", {"start": v(-9.74, 3.57) * mm, "end": v(-10.62, 2.64) * mm});
            skLineSegment(sketch, "E363", {"start": v(-10.62, 2.64) * mm, "end": v(-11.46, 1.68) * mm});
            skLineSegment(sketch, "E364", {"start": v(-11.46, 1.68) * mm, "end": v(-12.23, 0.66) * mm});
            skLineSegment(sketch, "E365", {"start": v(-12.23, 0.66) * mm, "end": v(-12.55, 0.18) * mm});
            skLineSegment(sketch, "E366", {"start": v(-12.55, 0.18) * mm, "end": v(-12.86, -0.32) * mm});
            skLineSegment(sketch, "E367", {"start": v(-12.86, -0.32) * mm, "end": v(-13.11, -0.84) * mm});
            skLineSegment(sketch, "E368", {"start": v(-13.11, -0.84) * mm, "end": v(-13.28, -1.41) * mm});
            skLineSegment(sketch, "E369", {"start": v(-13.28, -1.41) * mm, "end": v(-13.34, -2.02) * mm});
            skLineSegment(sketch, "E370", {"start": v(-13.34, -2.02) * mm, "end": v(-13.3, -2.81) * mm});
            skLineSegment(sketch, "E371", {"start": v(-13.3, -2.81) * mm, "end": v(-13.2, -3.6) * mm});
            skLineSegment(sketch, "E372", {"start": v(-13.2, -3.6) * mm, "end": v(-12.99, -4.8) * mm});
            skLineSegment(sketch, "E373", {"start": v(9.52, -6.21) * mm, "end": v(9.43, -6.13) * mm});
            skArc(sketch, "E374", {"start": v(13.36, -7.13) * mm, "mid": v(11.33, -7.12) * mm, "end": v(9.52, -6.21) * mm});
            skLineSegment(sketch, "E375", {"start": v(14.25, -6.93) * mm, "end": v(13.36, -7.13) * mm});
            skArc(sketch, "E376", {"start": v(18.16, -3.77) * mm, "mid": v(16.57, -5.8) * mm, "end": v(14.25, -6.93) * mm});
            skLineSegment(sketch, "E377", {"start": v(10.12, 15.29) * mm, "end": v(11.31, 13.93) * mm});
            skLineSegment(sketch, "E378", {"start": v(11.31, 13.93) * mm, "end": v(12.55, 12.62) * mm});
            skLineSegment(sketch, "E379", {"start": v(12.55, 12.62) * mm, "end": v(13.76, 11.32) * mm});
            skLineSegment(sketch, "E380", {"start": v(13.76, 11.32) * mm, "end": v(14.64, 10.3) * mm});
            skLineSegment(sketch, "E381", {"start": v(14.64, 10.3) * mm, "end": v(15.45, 9.22) * mm});
            skLineSegment(sketch, "E382", {"start": v(15.45, 9.22) * mm, "end": v(16.17, 8.08) * mm});
            skLineSegment(sketch, "E383", {"start": v(16.17, 8.08) * mm, "end": v(16.79, 6.88) * mm});
            skLineSegment(sketch, "E384", {"start": v(16.79, 6.88) * mm, "end": v(17.33, 5.52) * mm});
            skLineSegment(sketch, "E385", {"start": v(17.33, 5.52) * mm, "end": v(17.78, 4.11) * mm});
            skLineSegment(sketch, "E386", {"start": v(17.78, 4.11) * mm, "end": v(18.14, 2.67) * mm});
            skLineSegment(sketch, "E387", {"start": v(18.14, 2.67) * mm, "end": v(18.4, 1.2) * mm});
            skLineSegment(sketch, "E388", {"start": v(18.4, 1.2) * mm, "end": v(18.56, -0.25) * mm});
            skLineSegment(sketch, "E389", {"start": v(18.56, -0.25) * mm, "end": v(18.65, -1.7) * mm});
            skLineSegment(sketch, "E390", {"start": v(18.65, -1.7) * mm, "end": v(18.61, -2.32) * mm});
            skLineSegment(sketch, "E391", {"start": v(18.61, -2.32) * mm, "end": v(18.48, -2.93) * mm});
            skLineSegment(sketch, "E392", {"start": v(18.48, -2.93) * mm, "end": v(18.33, -3.36) * mm});
            skLineSegment(sketch, "E393", {"start": v(18.33, -3.36) * mm, "end": v(18.16, -3.77) * mm});
            skLineSegment(sketch, "E394", {"start": v(14.08, -3.37) * mm, "end": v(14.1, -3.28) * mm});
            skLineSegment(sketch, "E395", {"start": v(14.1, -3.28) * mm, "end": v(14.3, -2.66) * mm});
            skLineSegment(sketch, "E396", {"start": v(14.3, -2.66) * mm, "end": v(14.48, -2.04) * mm});
            skLineSegment(sketch, "E397", {"start": v(14.48, -2.04) * mm, "end": v(14.63, -1.4) * mm});
            skLineSegment(sketch, "E398", {"start": v(14.63, -1.4) * mm, "end": v(14.68, -0.75) * mm});
            skLineSegment(sketch, "E399", {"start": v(14.68, -0.75) * mm, "end": v(14.64, -0.34) * mm});
            skLineSegment(sketch, "E400", {"start": v(14.64, -0.34) * mm, "end": v(14.54, 0.06) * mm});
            skLineSegment(sketch, "E401", {"start": v(14.54, 0.06) * mm, "end": v(14.2, 0.85) * mm});
            skLineSegment(sketch, "E402", {"start": v(14.2, 0.85) * mm, "end": v(13.78, 1.59) * mm});
            skLineSegment(sketch, "E403", {"start": v(13.78, 1.59) * mm, "end": v(13.3, 2.3) * mm});
            skLineSegment(sketch, "E404", {"start": v(13.3, 2.3) * mm, "end": v(12.52, 3.34) * mm});
            skLineSegment(sketch, "E405", {"start": v(12.52, 3.34) * mm, "end": v(11.67, 4.35) * mm});
            skLineSegment(sketch, "E406", {"start": v(11.67, 4.35) * mm, "end": v(10.8, 5.33) * mm});
            skLineSegment(sketch, "E407", {"start": v(10.8, 5.33) * mm, "end": v(9.49, 6.8) * mm});
            skLineSegment(sketch, "E408", {"start": v(9.49, 6.8) * mm, "end": v(8.42, 8.15) * mm});
            skLineSegment(sketch, "E409", {"start": v(8.42, 8.15) * mm, "end": v(7.93, 8.85) * mm});
            skLineSegment(sketch, "E410", {"start": v(7.93, 8.85) * mm, "end": v(7.7, 9.23) * mm});
            skLineSegment(sketch, "E411", {"start": v(7.7, 9.23) * mm, "end": v(7.5, 9.62) * mm});
            skLineSegment(sketch, "E412", {"start": v(7.5, 9.62) * mm, "end": v(7.44, 9.85) * mm});
            skLineSegment(sketch, "E413", {"start": v(7.44, 9.85) * mm, "end": v(7.4, 10.08) * mm});
            skLineSegment(sketch, "E414", {"start": v(7.4, 10.08) * mm, "end": v(7.42, 10.32) * mm});
            skLineSegment(sketch, "E415", {"start": v(7.42, 10.32) * mm, "end": v(7.48, 10.55) * mm});
            skLineSegment(sketch, "E416", {"start": v(7.48, 10.55) * mm, "end": v(7.79, 11.35) * mm});
            skLineSegment(sketch, "E417", {"start": v(7.79, 11.35) * mm, "end": v(8.18, 12.13) * mm});
            skLineSegment(sketch, "E418", {"start": v(8.18, 12.13) * mm, "end": v(8.81, 13.19) * mm});
            skLineSegment(sketch, "E419", {"start": v(8.81, 13.19) * mm, "end": v(9.48, 14.23) * mm});
            skLineSegment(sketch, "E420", {"start": v(9.48, 14.23) * mm, "end": v(10.12, 15.29) * mm});
            skArc(sketch, "E421", {"start": v(12.52, -5) * mm, "mid": v(13.49, -4.37) * mm, "end": v(14.08, -3.37) * mm});
            skLineSegment(sketch, "E422", {"start": v(9.43, -6.13) * mm, "end": v(12.52, -5) * mm});
            skArc(sketch, "E423", {"start": v(-19.3, -23.57) * mm, "mid": v(-19.28, -23.63) * mm, "end": v(-19.21, -23.66) * mm});
            skLineSegment(sketch, "E424", {"start": v(-19.3, -23.57) * mm, "end": v(-19.3, -23.57) * mm});
            skCircle(sketch, "E425", {"center": v(1.02, 3.14) * mm, "radius": 27.94 * mm});
            skSolve(sketch);
        }
        {
            var Q0;
            Q0=makeQuery(id+"F0.imprint","IMPRINT",FACE,{"disambiguationData":[TD([[makeQuery(id+"F0.imprint","IMPRINT",EDGE,{"derivedFrom":sQuery(id+"F0.wireOp",EDGE,"E0")}),1.0]])]});
            var sketch = newSketch(context, id + "F1", { "sketchPlane" : qUnion([Q0])});
            skCircle(sketch, "E426", {"center": v(1.02, 3.14) * mm, "radius": 28.58 * mm});
            skSolve(sketch);
        }
        {
            var Q0;
            Q0 = qSketchRegion(id + "F1", true);
            extrude(context, id + "F2", {"entities" : qUnion([Q0]), "oppositeDirection" : true, "depth" : 27.94 * mm, "offsetDistance" : 25.4 * mm});
        }
        {
            var Q0;
            Q0=makeQuery(id+"F0.imprint","IMPRINT",FACE,{"disambiguationData":[TD([[makeQuery(id+"F0.imprint","IMPRINT",EDGE,{"derivedFrom":sQuery(id+"F0.wireOp",EDGE,"E0")}),1.0]])]});
            extrude(context, id + "F3", {"entities" : qUnion([Q0]), "operationType" : NewBodyOperationType.REMOVE, "oppositeDirection" : true, "depth" : 13.97 * mm, "offsetDistance" : 25.4 * mm});
        }
    });
